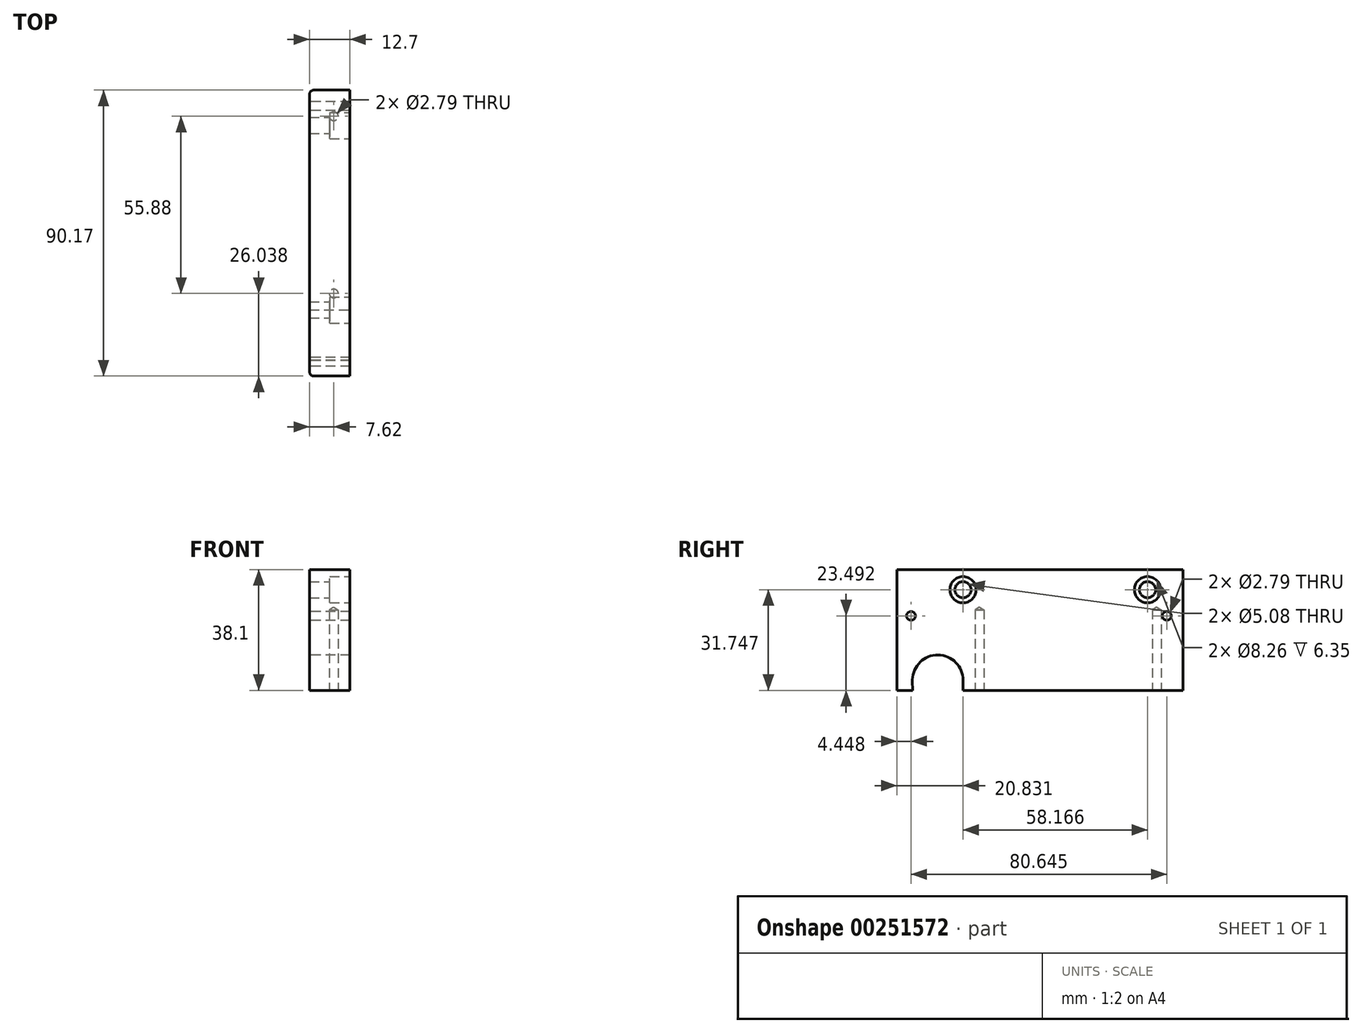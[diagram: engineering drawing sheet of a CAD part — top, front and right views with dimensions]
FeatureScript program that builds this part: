
annotation { "Feature Type Name" : "Feature", "Feature Type Description" : "" }
export const myFeature = defineFeature(function(context is Context, id is Id, definition is map)
    precondition{}
    {
        {
            var Q0;
            Q0=qCreatedBy(makeId("Right.planeOp"),FACE);
            var sketch = newSketch(context, id + "F0", { "sketchPlane" : qUnion([Q0])});
            skLineSegment(sketch, "E0.bottom", {"start": v(-25.35, 15.76) * mm, "end": v(64.82, 15.76) * mm});
            skLineSegment(sketch, "E0.top", {"start": v(-25.35, -22.34) * mm, "end": v(64.82, -22.34) * mm});
            skLineSegment(sketch, "E0.left", {"start": v(-25.35, 15.76) * mm, "end": v(-25.35, -22.34) * mm});
            skLineSegment(sketch, "E0.right", {"start": v(64.82, 15.76) * mm, "end": v(64.82, -22.34) * mm});
            skPoint(sketch, "E1", {"position": v(-20.9, 1.15) * mm});
            skPoint(sketch, "E2", {"position": v(59.74, 1.15) * mm});
            skPoint(sketch, "E3", {"position": v(-4.52, 9.4) * mm});
            skPoint(sketch, "E4", {"position": v(53.65, 9.4) * mm});
            skPoint(sketch, "E5", {"position": v(-12.52, -19.17) * mm});
            skSolve(sketch);
        }
        {
            var Q0;
            Q0 = qSketchRegion(id + "F0", true);
            extrude(context, id + "F1", {"entities" : qUnion([Q0]), "depth" : 12.7 * mm});
        }
        {
            var Q0;
            Q0=sQuery(id+"F0.wireOp",VERTEX,"E1");
            var Q1;
            Q1=sQuery(id+"F0.wireOp",VERTEX,"E2");
            var Q2;
            Q2=makeQuery(id+"F1.opExtrude","SWEPT_BODY",BODY,{"disambiguationData":[OSD([sQuery(id+"F0.wireOp",EDGE,"E0.bottom"),sQuery(id+"F0.wireOp",EDGE,"E0.top"),sQuery(id+"F0.wireOp",EDGE,"E0.left"),sQuery(id+"F0.wireOp",EDGE,"E0.right")])]});
            hole(context, id + "F2", {"style" : HoleStyle.SIMPLE, "endStyle" : HoleEndStyle.THROUGH, "oppositeDirection" : true, "holeDiameter" : 2.8 * mm, "isTappedThrough" : true, "tappedDepth" : 12.7 * mm, "tapClearance" : 3, "startFromSketch" : true, "locations" : qUnion([Q0, Q1]), "scope" : qUnion([Q2])});
        }
        {
            var Q0;
            Q0=makeQuery(id+"F1.opExtrude","CAP_FACE",FACE,{"disambiguationData":[OSD([sQuery(id+"F0.wireOp",EDGE,"E0.bottom"),sQuery(id+"F0.wireOp",EDGE,"E0.top"),sQuery(id+"F0.wireOp",EDGE,"E0.left"),sQuery(id+"F0.wireOp",EDGE,"E0.right")])],"isStart":false});
            var sketch = newSketch(context, id + "F3", { "sketchPlane" : qUnion([Q0])});
            skPoint(sketch, "E6", {"position": v(-4.52, 9.4) * mm});
            skPoint(sketch, "E7", {"position": v(53.65, 9.4) * mm});
            skSolve(sketch);
        }
        {
            var Q0;
            Q0=sQuery(id+"F3.wireOp",VERTEX,"E6");
            var Q1;
            Q1=sQuery(id+"F3.wireOp",VERTEX,"E7");
            var Q2;
            Q2=makeQuery(id+"F1.opExtrude","SWEPT_BODY",BODY,{"disambiguationData":[OSD([sQuery(id+"F0.wireOp",EDGE,"E0.bottom"),sQuery(id+"F0.wireOp",EDGE,"E0.top"),sQuery(id+"F0.wireOp",EDGE,"E0.left"),sQuery(id+"F0.wireOp",EDGE,"E0.right")])]});
            hole(context, id + "F4", {"style" : HoleStyle.C_BORE, "endStyle" : HoleEndStyle.THROUGH, "holeDiameter" : 5.08 * mm, "cBoreDiameter" : 8.25 * mm, "cBoreDepth" : 6.35 * mm, "isTappedThrough" : true, "tappedDepth" : 12.7 * mm, "tapClearance" : 3, "startFromSketch" : true, "locations" : qUnion([Q0, Q1]), "scope" : qUnion([Q2])});
        }
        {
            var Q0;
            Q0=qCreatedBy(makeId("Right.planeOp"),FACE);
            var sketch = newSketch(context, id + "F5", { "sketchPlane" : qUnion([Q0])});
            skArc(sketch, "E8", {"start": v(-20.45, -18.97) * mm, "mid": v(-20.46, -19.17) * mm, "end": v(-20.45, -19.36) * mm});
            skLineSegment(sketch, "E9", {"start": v(-20.45, -19.36) * mm, "end": v(-20.38, -22.57) * mm});
            skLineSegment(sketch, "E10", {"start": v(-20.38, -22.57) * mm, "end": v(-4.5, -22.57) * mm});
            skLineSegment(sketch, "E11", {"start": v(-4.5, -22.57) * mm, "end": v(-4.5, -19.17) * mm});
            skArc(sketch, "E12", {"start": v(-4.5, -19.17) * mm, "mid": v(-12.58, -11.19) * mm, "end": v(-20.45, -19.36) * mm});
            skSolve(sketch);
        }
        {
            var Q0;
            Q0 = qSketchRegion(id + "F5", true);
            extrude(context, id + "F6", {"entities" : qUnion([Q0]), "operationType" : NewBodyOperationType.REMOVE, "endBound" : BoundingType.THROUGH_ALL, "depth" : 25.4 * mm});
        }
        {
            var Q0;
            {var subQ0=sQuery(id+"F0.wireOp",EDGE,"E0.right");var subQ2=sQuery(id+"F0.wireOp",EDGE,"E0.top");Q0=makeQuery(id+"F6.boolean.opBoolean","SPLIT",FACE,{"disambiguationData":[TD([makeQuery(id+"F1.opExtrude","SWEPT_FACE",FACE,{"disambiguationData":[OSD([subQ0])]})])],"derivedFrom":makeQuery(id+"F1.opExtrude","SWEPT_FACE",FACE,{"disambiguationData":[OSD([subQ2])]})});}
            var sketch = newSketch(context, id + "F7", { "sketchPlane" : qUnion([Q0])});
            skPoint(sketch, "E13", {"position": v(7.62, -56.57) * mm});
            skPoint(sketch, "E14", {"position": v(7.62, -0.69) * mm});
            skSolve(sketch);
        }
        {
            var Q0;
            Q0=sQuery(id+"F7.wireOp",VERTEX,"E14");
            var Q1;
            Q1=sQuery(id+"F7.wireOp",VERTEX,"E13");
            var Q2;
            Q2=makeQuery(id+"F1.opExtrude","SWEPT_BODY",BODY,{"disambiguationData":[OSD([sQuery(id+"F0.wireOp",EDGE,"E0.bottom"),sQuery(id+"F0.wireOp",EDGE,"E0.top"),sQuery(id+"F0.wireOp",EDGE,"E0.left"),sQuery(id+"F0.wireOp",EDGE,"E0.right")])]});
            hole(context, id + "F8", {"style" : HoleStyle.SIMPLE, "endStyle" : HoleEndStyle.BLIND, "holeDiameter" : 2.8 * mm, "holeDepth" : 25.4 * mm, "isTappedThrough" : true, "tappedDepth" : 12.7 * mm, "tapClearance" : 3, "startFromSketch" : true, "locations" : qUnion([Q0, Q1]), "scope" : qUnion([Q2])});
        }
        {
            var Q0;
            Q0=makeQuery(id+"F1.opExtrude","CAP_EDGE",EDGE,{"disambiguationData":[OSD([sQuery(id+"F0.wireOp",EDGE,"E0.left")])],"isStart":true});
            var Q1;
            Q1=makeQuery(id+"F1.opExtrude","CAP_EDGE",EDGE,{"disambiguationData":[OSD([sQuery(id+"F0.wireOp",EDGE,"E0.right")])],"isStart":true});
            fillet(context, id + "F9", {"entities" : qUnion([Q0, Q1]), "radius" : 1.27 * mm, "tangentPropagation" : true, "allowEdgeOverflow" : false});
        }
    });
